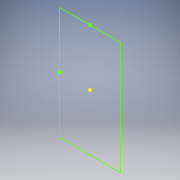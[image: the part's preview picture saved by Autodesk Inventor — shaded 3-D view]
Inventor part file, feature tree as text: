
AUTODESK INVENTOR PART (.ipt)
format: ipt  version: 2018 (Build 220112000, 112)  size: 83,456 bytes
history: native  units: mm
features: sketch x1
ambient origin geometry x8: Origin, YZ Plane, XZ Plane, XY Plane, X Axis, Y Axis, Z Axis, Center Point
feature tree (1):
  sketch  "Sketch1"
